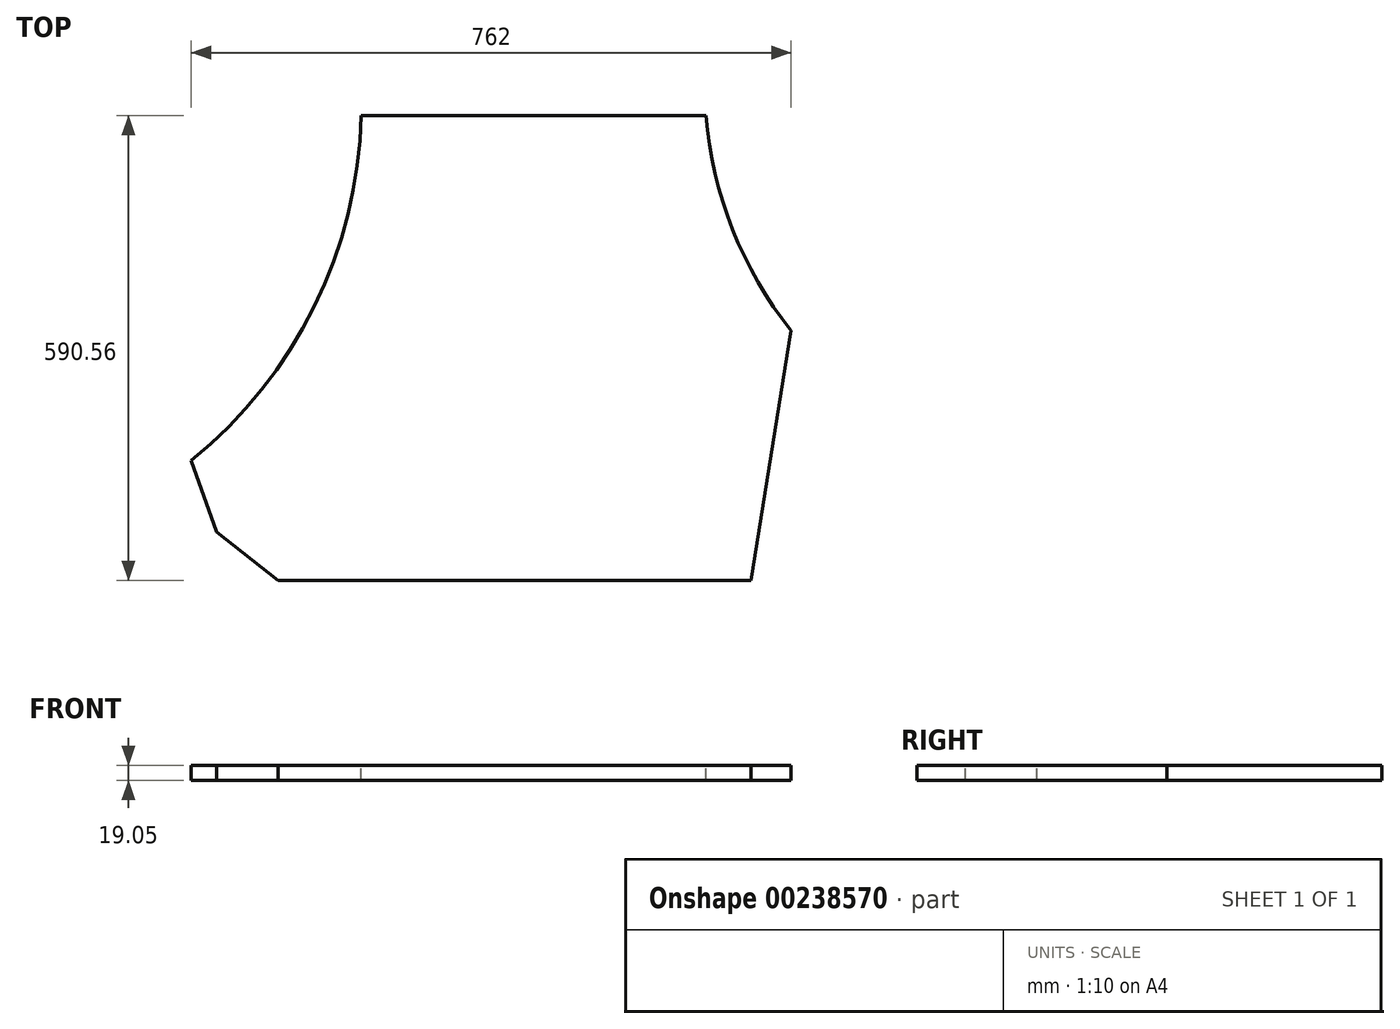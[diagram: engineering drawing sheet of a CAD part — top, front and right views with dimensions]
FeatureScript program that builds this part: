
annotation { "Feature Type Name" : "Feature", "Feature Type Description" : "" }
export const myFeature = defineFeature(function(context is Context, id is Id, definition is map)
    precondition{}
    {
        {
            var Q0;
            Q0=qCreatedBy(makeId("Top.planeOp"),FACE);
            var sketch = newSketch(context, id + "F0", { "sketchPlane" : qUnion([Q0])});
            skLineSegment(sketch, "E0.bottom", {"start": v(381, -295.28) * mm, "end": v(-381, -295.28) * mm});
            skLineSegment(sketch, "E0.top", {"start": v(381, 295.28) * mm, "end": v(-381, 295.28) * mm});
            skLineSegment(sketch, "E0.left", {"start": v(381, -295.28) * mm, "end": v(381, 295.28) * mm});
            skLineSegment(sketch, "E0.right", {"start": v(-381, -295.28) * mm, "end": v(-381, 295.27) * mm});
            skPoint(sketch, "E0.middle", {"position": v(0, 0) * mm});
            skSolve(sketch);
        }
        {
            var Q0;
            Q0=makeQuery(id+"F0.imprint","IMPRINT",FACE,{"disambiguationData":[TD([[makeQuery(id+"F0.imprint","IMPRINT",EDGE,{"derivedFrom":sQuery(id+"F0.wireOp",EDGE,"E0.bottom")}),-1.0]])]});
            extrude(context, id + "F1", {"entities" : qUnion([Q0]), "depth" : 19.05 * mm});
        }
        {
            var Q0;
            Q0=makeQuery(id+"F1.opExtrude","CAP_FACE",FACE,{"disambiguationData":[OSD([sQuery(id+"F0.wireOp",EDGE,"E0.bottom"),sQuery(id+"F0.wireOp",EDGE,"E0.top"),sQuery(id+"F0.wireOp",EDGE,"E0.left"),sQuery(id+"F0.wireOp",EDGE,"E0.right")])],"isStart":false});
            var sketch = newSketch(context, id + "F2", { "sketchPlane" : qUnion([Q0])});
            skLineSegment(sketch, "E1", {"start": v(273.05, 295.28) * mm, "end": v(273.05, -295.28) * mm});
            skLineSegment(sketch, "E2", {"start": v(-165.1, 295.28) * mm, "end": v(-165.1, -295.28) * mm});
            skLineSegment(sketch, "E3", {"start": v(-381, -295.28) * mm, "end": v(-381, -142.88) * mm});
            skLineSegment(sketch, "E4", {"start": v(-381, -142.88) * mm, "end": v(-381, 295.27) * mm});
            skArc(sketch, "E5", {"start": v(-381, -142.88) * mm, "mid": v(-224.9, 52.48) * mm, "end": v(-165.1, 295.27) * mm});
            skPoint(sketch, "E5.third.point", {"position": v(-187.73, 471.35) * mm});
            skSolve(sketch);
        }
        {
            var Q0;
            {var subQ0=sQuery(id+"F2.wireOp",EDGE,"E4");Q0=makeQuery(id+"F2.imprint","IMPRINT",FACE,{"disambiguationData":[TD([[makeQuery(id+"F2.imprint","IMPRINT",EDGE,{"derivedFrom":subQ0}),-1.0]])]});}
            extrude(context, id + "F3", {"entities" : qUnion([Q0]), "operationType" : NewBodyOperationType.REMOVE, "oppositeDirection" : true, "depth" : 25.4 * mm});
        }
        {
            var Q0;
            Q0=makeQuery(id+"F1.opExtrude","CAP_FACE",FACE,{"disambiguationData":[OSD([sQuery(id+"F0.wireOp",EDGE,"E0.bottom"),sQuery(id+"F0.wireOp",EDGE,"E0.top"),sQuery(id+"F0.wireOp",EDGE,"E0.left"),sQuery(id+"F0.wireOp",EDGE,"E0.right")])],"isStart":false});
            var sketch = newSketch(context, id + "F4", { "sketchPlane" : qUnion([Q0])});
            skLineSegment(sketch, "E6", {"start": v(381, 295.28) * mm, "end": v(381, 22.22) * mm});
            skLineSegment(sketch, "E7", {"start": v(381, 295.28) * mm, "end": v(273.05, 295.28) * mm});
            skArc(sketch, "E8", {"start": v(273.05, 295.27) * mm, "mid": v(306.44, 150.61) * mm, "end": v(381, 22.22) * mm});
            skPoint(sketch, "E8.third.point", {"position": v(803.98, -163) * mm});
            skSolve(sketch);
        }
        {
            var Q0;
            Q0=makeQuery(id+"F4.imprint","IMPRINT",FACE,{"disambiguationData":[TD([[makeQuery(id+"F4.imprint","IMPRINT",EDGE,{"derivedFrom":sQuery(id+"F4.wireOp",EDGE,"E6")}),1.0]])]});
            extrude(context, id + "F5", {"entities" : qUnion([Q0]), "operationType" : NewBodyOperationType.REMOVE, "oppositeDirection" : true, "depth" : 25.4 * mm});
        }
        {
            var Q0;
            Q0=makeQuery(id+"F1.opExtrude","CAP_FACE",FACE,{"disambiguationData":[OSD([sQuery(id+"F0.wireOp",EDGE,"E0.bottom"),sQuery(id+"F0.wireOp",EDGE,"E0.top"),sQuery(id+"F0.wireOp",EDGE,"E0.left"),sQuery(id+"F0.wireOp",EDGE,"E0.right")])],"isStart":false});
            var sketch = newSketch(context, id + "F6", { "sketchPlane" : qUnion([Q0])});
            skLineSegment(sketch, "E9", {"start": v(381, 22.23) * mm, "end": v(330.2, -295.28) * mm});
            skLineSegment(sketch, "E10", {"start": v(330.2, -295.28) * mm, "end": v(381, -295.28) * mm});
            skLineSegment(sketch, "E11", {"start": v(381, -295.28) * mm, "end": v(381, 22.22) * mm});
            skSolve(sketch);
        }
        {
            var Q0;
            Q0=makeQuery(id+"F6.imprint","IMPRINT",FACE,{"disambiguationData":[TD([[makeQuery(id+"F6.imprint","IMPRINT",EDGE,{"derivedFrom":sQuery(id+"F6.wireOp",EDGE,"E9")}),1.0]])]});
            extrude(context, id + "F7", {"entities" : qUnion([Q0]), "operationType" : NewBodyOperationType.REMOVE, "oppositeDirection" : true, "depth" : 25.4 * mm});
        }
        {
            var Q0;
            Q0=makeQuery(id+"F1.opExtrude","CAP_FACE",FACE,{"disambiguationData":[OSD([sQuery(id+"F0.wireOp",EDGE,"E0.bottom"),sQuery(id+"F0.wireOp",EDGE,"E0.top"),sQuery(id+"F0.wireOp",EDGE,"E0.left"),sQuery(id+"F0.wireOp",EDGE,"E0.right")])],"isStart":false});
            var sketch = newSketch(context, id + "F8", { "sketchPlane" : qUnion([Q0])});
            skLineSegment(sketch, "E12", {"start": v(-381, -142.88) * mm, "end": v(-349.16, -233.9) * mm});
            skLineSegment(sketch, "E13", {"start": v(-349.16, -233.9) * mm, "end": v(-270.69, -295.28) * mm});
            skLineSegment(sketch, "E14", {"start": v(-270.69, -295.28) * mm, "end": v(-381, -295.28) * mm});
            skSolve(sketch);
        }
        {
            var Q0;
            Q0=makeQuery(id+"F8.imprint","IMPRINT",FACE,{"disambiguationData":[TD([[makeQuery(id+"F8.imprint","IMPRINT",EDGE,{"derivedFrom":sQuery(id+"F8.wireOp",EDGE,"E12")}),-1.0]])]});
            extrude(context, id + "F9", {"entities" : qUnion([Q0]), "operationType" : NewBodyOperationType.REMOVE, "oppositeDirection" : true, "depth" : 25.4 * mm});
        }
    });
